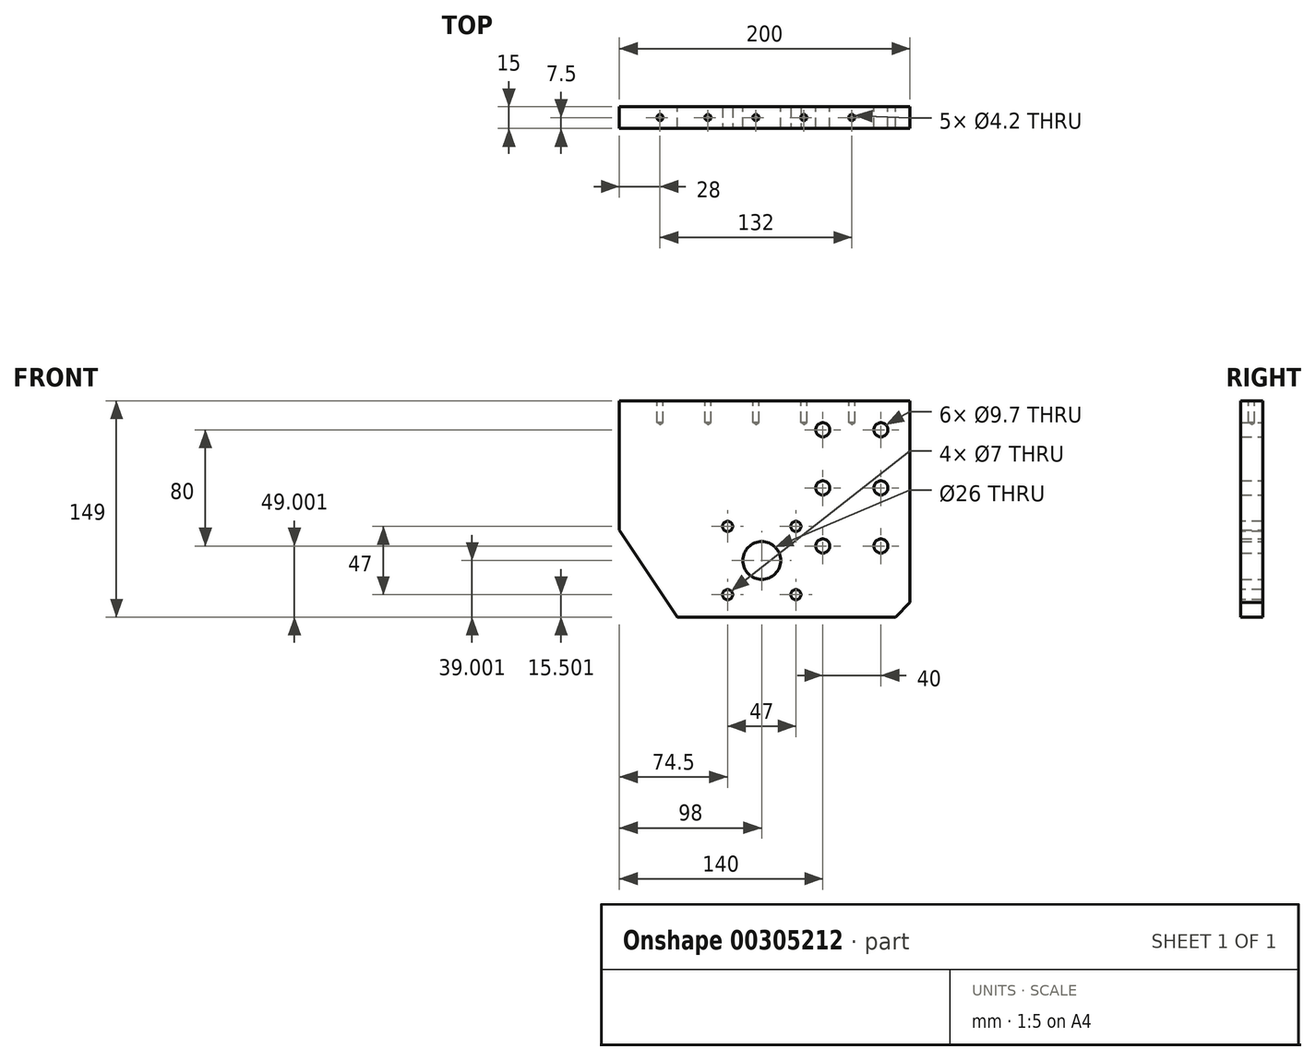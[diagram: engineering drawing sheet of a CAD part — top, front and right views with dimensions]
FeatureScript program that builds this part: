
annotation { "Feature Type Name" : "Feature", "Feature Type Description" : "" }
export const myFeature = defineFeature(function(context is Context, id is Id, definition is map)
    precondition{}
    {
        {
            var Q0;
            Q0=qCreatedBy(makeId("Front.planeOp"),FACE);
            var sketch = newSketch(context, id + "F0", { "sketchPlane" : qUnion([Q0])});
            skLineSegment(sketch, "E0.0.0", {"start": v(73.43, 89.57) * mm, "end": v(-48.57, 89.57) * mm});
            skLineSegment(sketch, "E0.0.2", {"start": v(-67.57, 29.57) * mm, "end": v(-67.57, -59.43) * mm});
            skLineSegment(sketch, "E0.0.3", {"start": v(-67.57, -59.43) * mm, "end": v(63.43, -59.43) * mm});
            skLineSegment(sketch, "E0.0.4", {"start": v(63.43, -59.43) * mm, "end": v(73.43, -49.43) * mm});
            skLineSegment(sketch, "E0.0.5", {"start": v(73.43, -49.43) * mm, "end": v(73.43, 89.57) * mm});
            skCircle(sketch, "E1", {"center": v(-28.57, -20.43) * mm, "radius": 13 * mm});
            skLineSegment(sketch, "E2", {"start": v(-67.57, 29.57) * mm, "end": v(-67.57, 89.57) * mm});
            skLineSegment(sketch, "E3", {"start": v(-67.57, 89.57) * mm, "end": v(-48.57, 89.57) * mm});
            skSolve(sketch);
        }
        {
            var Q0;
            Q0=makeQuery(id+"F0.imprint","IMPRINT",FACE,{"disambiguationData":[TD([[makeQuery(id+"F0.imprint","IMPRINT",EDGE,{"derivedFrom":sQuery(id+"F0.wireOp",EDGE,"E0.0.0")}),1.0]])]});
            var Q1;
            Q1=sQuery(id+"F0.wireOp",EDGE,"E0.0.0");
            var Q2;
            Q2=sQuery(id+"F0.wireOp",EDGE,"E0.0.1");
            var Q3;
            Q3=sQuery(id+"F0.wireOp",EDGE,"E0.0.2");
            var Q4;
            Q4=sQuery(id+"F0.wireOp",EDGE,"E0.0.3");
            var Q5;
            Q5=sQuery(id+"F0.wireOp",EDGE,"E0.0.4");
            var Q6;
            Q6=sQuery(id+"F0.wireOp",EDGE,"E0.0.5");
            var Q7;
            Q7=sQuery(id+"F0.wireOp",EDGE,"f17e8e4c-c160-46d6-aea5-5cb9cd516dda.0");
            extrude(context, id + "F1", {"entities" : qUnion([Q0]), "surfaceEntities" : qUnion([Q1, Q2, Q3, Q4, Q5, Q6, Q7]), "depth" : 15 * mm});
        }
        {
            var Q0;
            Q0=makeQuery(id+"F1.opExtrude","CAP_FACE",FACE,{"disambiguationData":[OSD([sQuery(id+"F0.wireOp",EDGE,"E0.0.0"),sQuery(id+"F0.wireOp",EDGE,"E0.0.1"),sQuery(id+"F0.wireOp",EDGE,"E0.0.2"),sQuery(id+"F0.wireOp",EDGE,"E0.0.3"),sQuery(id+"F0.wireOp",EDGE,"E0.0.4"),sQuery(id+"F0.wireOp",EDGE,"E0.0.5"),sQuery(id+"F0.wireOp",EDGE,"E1")])],"isStart":true});
            var sketch = newSketch(context, id + "F2", { "sketchPlane" : qUnion([Q0])});
            skCircle(sketch, "E4", {"center": v(-53.43, -10.43) * mm, "radius": 4.5 * mm});
            skPoint(sketch, "E5", {"position": v(-53.43, 29.57) * mm});
            skPoint(sketch, "E6", {"position": v(-53.43, 69.57) * mm});
            skPoint(sketch, "E7", {"position": v(-13.43, 69.57) * mm});
            skPoint(sketch, "E8", {"position": v(-13.43, 29.57) * mm});
            skPoint(sketch, "E9", {"position": v(-13.43, -10.43) * mm});
            skSolve(sketch);
        }
        {
            var Q0;
            Q0=sQuery(id+"F2.wireOp",VERTEX,"E4.center");
            var Q1;
            Q1=sQuery(id+"F2.wireOp",VERTEX,"E5");
            var Q2;
            Q2=sQuery(id+"F2.wireOp",VERTEX,"E6");
            var Q3;
            Q3=sQuery(id+"F2.wireOp",VERTEX,"E7");
            var Q4;
            Q4=sQuery(id+"F2.wireOp",VERTEX,"E8");
            var Q5;
            Q5=sQuery(id+"F2.wireOp",VERTEX,"E9");
            var Q6;
            Q6=makeQuery(id+"F1.opExtrude","SWEPT_BODY",BODY,{"disambiguationData":[OSD([sQuery(id+"F0.wireOp",EDGE,"E0.0.0"),sQuery(id+"F0.wireOp",EDGE,"E0.0.1"),sQuery(id+"F0.wireOp",EDGE,"E0.0.2"),sQuery(id+"F0.wireOp",EDGE,"E0.0.3"),sQuery(id+"F0.wireOp",EDGE,"E0.0.4"),sQuery(id+"F0.wireOp",EDGE,"E0.0.5"),sQuery(id+"F0.wireOp",EDGE,"E1")])]});
            hole(context, id + "F3", {"style" : HoleStyle.SIMPLE, "endStyle" : HoleEndStyle.THROUGH, "holeDiameter" : 9.7 * mm, "tappedDepth" : 12.6 * mm, "tapClearance" : 3, "startFromSketch" : true, "locations" : qUnion([Q0, Q1, Q2, Q3, Q4, Q5]), "scope" : qUnion([Q6]), "majorDiameter" : 5 * mm});
        }
        {
            var Q0;
            Q0=makeQuery(id+"F1.opExtrude","CAP_FACE",FACE,{"disambiguationData":[OSD([sQuery(id+"F0.wireOp",EDGE,"E0.0.0"),sQuery(id+"F0.wireOp",EDGE,"E0.0.1"),sQuery(id+"F0.wireOp",EDGE,"E0.0.2"),sQuery(id+"F0.wireOp",EDGE,"E0.0.3"),sQuery(id+"F0.wireOp",EDGE,"E0.0.4"),sQuery(id+"F0.wireOp",EDGE,"E0.0.5"),sQuery(id+"F0.wireOp",EDGE,"E1")])],"isStart":false});
            var sketch = newSketch(context, id + "F4", { "sketchPlane" : qUnion([Q0])});
            skPoint(sketch, "E10", {"position": v(-52.07, 3.07) * mm});
            skPoint(sketch, "E11", {"position": v(-5.07, 3.07) * mm});
            skPoint(sketch, "E12", {"position": v(-5.07, -43.93) * mm});
            skPoint(sketch, "E13", {"position": v(-52.07, -43.93) * mm});
            skSolve(sketch);
        }
        {
            var Q0;
            Q0=sQuery(id+"F4.wireOp",VERTEX,"E10");
            var Q1;
            Q1=sQuery(id+"F4.wireOp",VERTEX,"E13");
            var Q2;
            Q2=sQuery(id+"F4.wireOp",VERTEX,"E12");
            var Q3;
            Q3=sQuery(id+"F4.wireOp",VERTEX,"E11");
            var Q4;
            Q4=makeQuery(id+"F1.opExtrude","SWEPT_BODY",BODY,{"disambiguationData":[OSD([sQuery(id+"F0.wireOp",EDGE,"E0.0.0"),sQuery(id+"F0.wireOp",EDGE,"E0.0.1"),sQuery(id+"F0.wireOp",EDGE,"E0.0.2"),sQuery(id+"F0.wireOp",EDGE,"E0.0.3"),sQuery(id+"F0.wireOp",EDGE,"E0.0.4"),sQuery(id+"F0.wireOp",EDGE,"E0.0.5"),sQuery(id+"F0.wireOp",EDGE,"E1")])]});
            hole(context, id + "F5", {"style" : HoleStyle.SIMPLE, "endStyle" : HoleEndStyle.THROUGH, "holeDiameter" : 7 * mm, "tappedDepth" : 12.6 * mm, "tapClearance" : 3, "startFromSketch" : true, "locations" : qUnion([Q0, Q1, Q2, Q3]), "scope" : qUnion([Q4])});
        }
        {
            var Q0;
            Q0=makeQuery(id+"F1.opExtrude","SWEPT_FACE",FACE,{"disambiguationData":[OSD([sQuery(id+"F0.wireOp",EDGE,"E0.0.2"),sQuery(id+"F0.wireOp",EDGE,"E2")])]});
            extrude(context, id + "F6", {"entities" : qUnion([Q0]), "operationType" : NewBodyOperationType.ADD, "depth" : 4 * mm});
        }
        {
            var Q0;
            Q0=makeQuery(id+"F6.opExtrude","CAP_FACE",FACE,{"disambiguationData":[OSD([sQuery(id+"F0.wireOp",EDGE,"E0.0.2"),sQuery(id+"F0.wireOp",EDGE,"E2")])],"isStart":false});
            extrude(context, id + "F7", {"entities" : qUnion([Q0]), "operationType" : NewBodyOperationType.ADD, "depth" : 55 * mm});
        }
        {
            var Q0;
            {var subQ0=sQuery(id+"F0.wireOp",EDGE,"E2");var subQ1=sQuery(id+"F0.wireOp",EDGE,"E0.0.2");var subQ2=makeQuery(id+"F1.opExtrude","CAP_EDGE",EDGE,{"disambiguationData":[OSD([subQ1,subQ0])],"isStart":true});Q0=makeQuery(id+"F7.boolean.opBoolean","MERGE",FACE,{"derivedFrom":[makeQuery(id+"F6.boolean.opBoolean","MERGE",FACE,{"derivedFrom":[makeQuery(id+"F1.opExtrude","CAP_FACE",FACE,{"disambiguationData":[OSD([sQuery(id+"F0.wireOp",EDGE,"E0.0.0"),subQ1,sQuery(id+"F0.wireOp",EDGE,"E0.0.3"),sQuery(id+"F0.wireOp",EDGE,"E0.0.4"),sQuery(id+"F0.wireOp",EDGE,"E0.0.5"),sQuery(id+"F0.wireOp",EDGE,"E1"),subQ0,sQuery(id+"F0.wireOp",EDGE,"E3")])],"isStart":true}),makeQuery(id+"F6.opExtrude","SWEPT_FACE",FACE,{"disambiguationData":[OSD([subQ1,subQ0]),TDD([subQ2])]})]}),makeQuery(id+"F7.opExtrude","SWEPT_FACE",FACE,{"disambiguationData":[OSD([subQ1,subQ0]),TDD([makeQuery(id+"F6.opExtrude","CAP_EDGE",EDGE,{"disambiguationData":[OSD([subQ1,subQ0]),TDD([subQ2])],"isStart":false})])]})]});}
            var sketch = newSketch(context, id + "F8", { "sketchPlane" : qUnion([Q0])});
            skPoint(sketch, "E14", {"position": v(126.57, 0.57) * mm});
            skPoint(sketch, "E15", {"position": v(86.57, -59.43) * mm});
            skLineSegment(sketch, "E16", {"start": v(126.57, 0.57) * mm, "end": v(86.57, -59.43) * mm});
            skSolve(sketch);
        }
        {
            var Q0;
            {var subQ0=sQuery(id+"F8.wireOp",EDGE,"E16");Q0=makeQuery(id+"F8.imprint","IMPRINT",FACE,{"disambiguationData":[TD([[makeQuery(id+"F8.imprint","IMPRINT",EDGE,{"derivedFrom":subQ0}),1.0]])]});}
            extrude(context, id + "F9", {"entities" : qUnion([Q0]), "operationType" : NewBodyOperationType.REMOVE, "oppositeDirection" : true, "depth" : 25 * mm});
        }
        {
            var Q0;
            {var subQ0=sQuery(id+"F0.wireOp",EDGE,"E3");var subQ1=sQuery(id+"F0.wireOp",EDGE,"E2");Q0=makeQuery(id+"F7.boolean.opBoolean","MERGE",FACE,{"derivedFrom":[makeQuery(id+"F6.boolean.opBoolean","MERGE",FACE,{"derivedFrom":[makeQuery(id+"F1.opExtrude","SWEPT_FACE",FACE,{"disambiguationData":[OSD([sQuery(id+"F0.wireOp",EDGE,"E0.0.0"),subQ0])]}),makeQuery(id+"F6.opExtrude","SWEPT_FACE",FACE,{"disambiguationData":[OSD([subQ1,subQ0])]})]}),makeQuery(id+"F7.opExtrude","SWEPT_FACE",FACE,{"disambiguationData":[OSD([subQ1,subQ0])]})]});}
            var sketch = newSketch(context, id + "F10", { "sketchPlane" : qUnion([Q0])});
            skPoint(sketch, "E17", {"position": v(33.43, -7.5) * mm});
            skPoint(sketch, "E18", {"position": v(0.43, -7.5) * mm});
            skPoint(sketch, "E19", {"position": v(-98.57, -7.5) * mm});
            skPoint(sketch, "E20", {"position": v(-32.57, -7.5) * mm});
            skPoint(sketch, "E21", {"position": v(-65.57, -7.5) * mm});
            skSolve(sketch);
        }
        {
            var Q0;
            Q0=sQuery(id+"F10.wireOp",VERTEX,"E19");
            var Q1;
            Q1=sQuery(id+"F10.wireOp",VERTEX,"E21");
            var Q2;
            Q2=sQuery(id+"F10.wireOp",VERTEX,"E20");
            var Q3;
            Q3=sQuery(id+"F10.wireOp",VERTEX,"E18");
            var Q4;
            Q4=sQuery(id+"F10.wireOp",VERTEX,"E17");
            var Q5;
            Q5=makeQuery(id+"F1.opExtrude","SWEPT_BODY",BODY,{"disambiguationData":[OSD([sQuery(id+"F0.wireOp",EDGE,"E0.0.0"),sQuery(id+"F0.wireOp",EDGE,"E0.0.2"),sQuery(id+"F0.wireOp",EDGE,"E0.0.3"),sQuery(id+"F0.wireOp",EDGE,"E0.0.4"),sQuery(id+"F0.wireOp",EDGE,"E0.0.5"),sQuery(id+"F0.wireOp",EDGE,"E1"),sQuery(id+"F0.wireOp",EDGE,"E2"),sQuery(id+"F0.wireOp",EDGE,"E3")])]});
            hole(context, id + "F11", {"style" : HoleStyle.SIMPLE, "endStyle" : HoleEndStyle.BLIND, "standardTappedOrClearance" : lookupTablePath({ "standard" : "ISO", "engagement" : "75%", "pitch" : "0.8 mm", "size" : "M5", "type" : "Tapped" }), "standardBlindInLast" : lookupTablePath({ "standard" : "ISO", "engagement" : "75%", "pitch" : "0.8 mm", "size" : "M5", "type" : "Tapped" }), "holeDiameter" : 4.2 * mm, "showTappedDepth" : true, "holeDepth" : 15 * mm, "tappedDepth" : 12.6 * mm, "tapClearance" : 3, "startFromSketch" : true, "locations" : qUnion([Q0, Q1, Q2, Q3, Q4]), "scope" : qUnion([Q5]), "majorDiameter" : 5 * mm});
        }
    });
